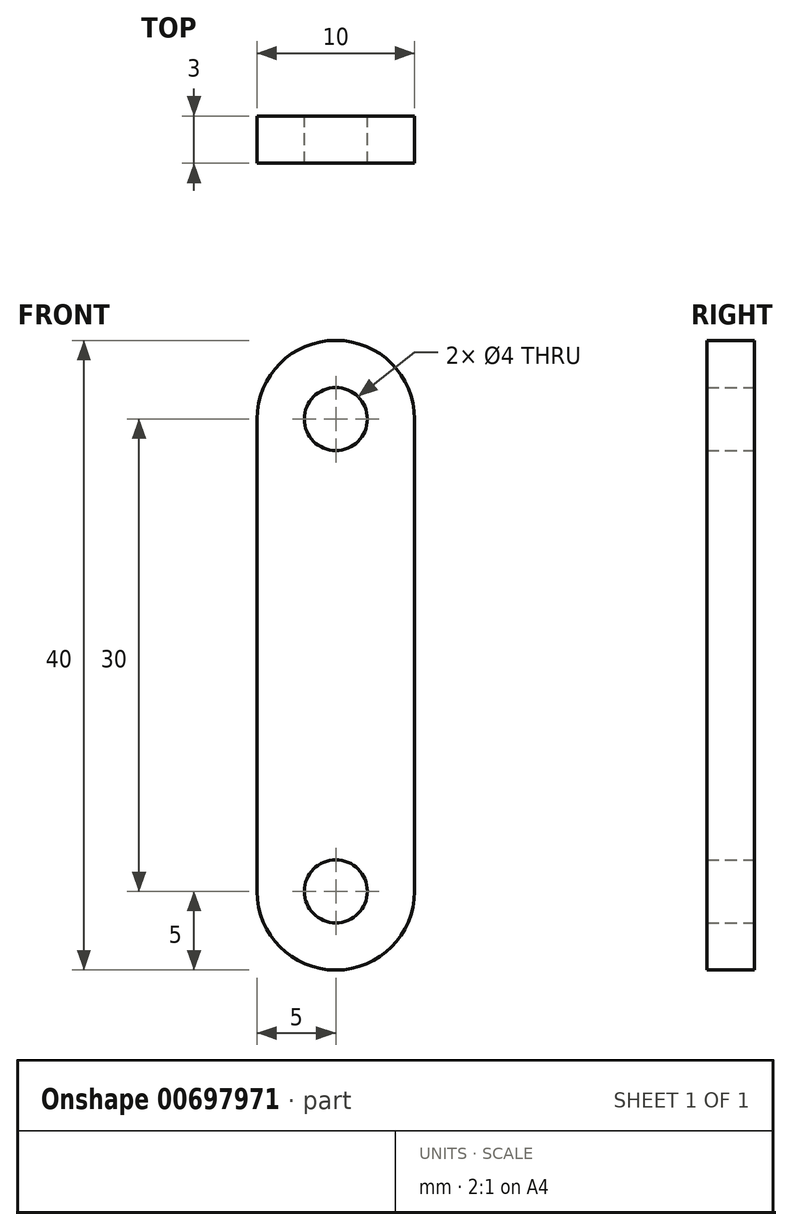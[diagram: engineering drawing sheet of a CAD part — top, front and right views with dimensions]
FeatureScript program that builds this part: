
annotation { "Feature Type Name" : "Feature", "Feature Type Description" : "" }
export const myFeature = defineFeature(function(context is Context, id is Id, definition is map)
    precondition{}
    {
        {
            var Q0;
            Q0=qCreatedBy(makeId("Front.planeOp"),FACE);
            var sketch = newSketch(context, id + "F0", { "sketchPlane" : qUnion([Q0])});
            skLineSegment(sketch, "E0.bottom", {"start": v(5, 15) * mm, "end": v(-5, 15) * mm, "construction": true});
            skLineSegment(sketch, "E0.top", {"start": v(5, -15) * mm, "end": v(-5, -15) * mm, "construction": true});
            skLineSegment(sketch, "E0.left", {"start": v(5, 15) * mm, "end": v(5, -15) * mm});
            skLineSegment(sketch, "E0.right", {"start": v(-5, 15) * mm, "end": v(-5, -15) * mm});
            skPoint(sketch, "E0.middle", {"position": v(0, 0) * mm});
            skArc(sketch, "E1", {"start": v(5, 15) * mm, "mid": v(0, 20) * mm, "end": v(-5, 15) * mm});
            skArc(sketch, "E2", {"start": v(-5, -15) * mm, "mid": v(0, -20) * mm, "end": v(5, -15) * mm});
            skCircle(sketch, "E3", {"center": v(0, 15) * mm, "radius": 2 * mm});
            skCircle(sketch, "E4", {"center": v(0, -15) * mm, "radius": 2 * mm});
            skSolve(sketch);
        }
        {
            var Q0;
            Q0=makeQuery(id+"F0.imprint","IMPRINT",FACE,{"disambiguationData":[TD([[makeQuery(id+"F0.imprint","IMPRINT",EDGE,{"derivedFrom":sQuery(id+"F0.wireOp",EDGE,"E0.left")}),-1.0]])]});
            extrude(context, id + "F1", {"entities" : qUnion([Q0]), "depth" : 3 * mm, "offsetDistance" : 25 * mm});
        }
    });
